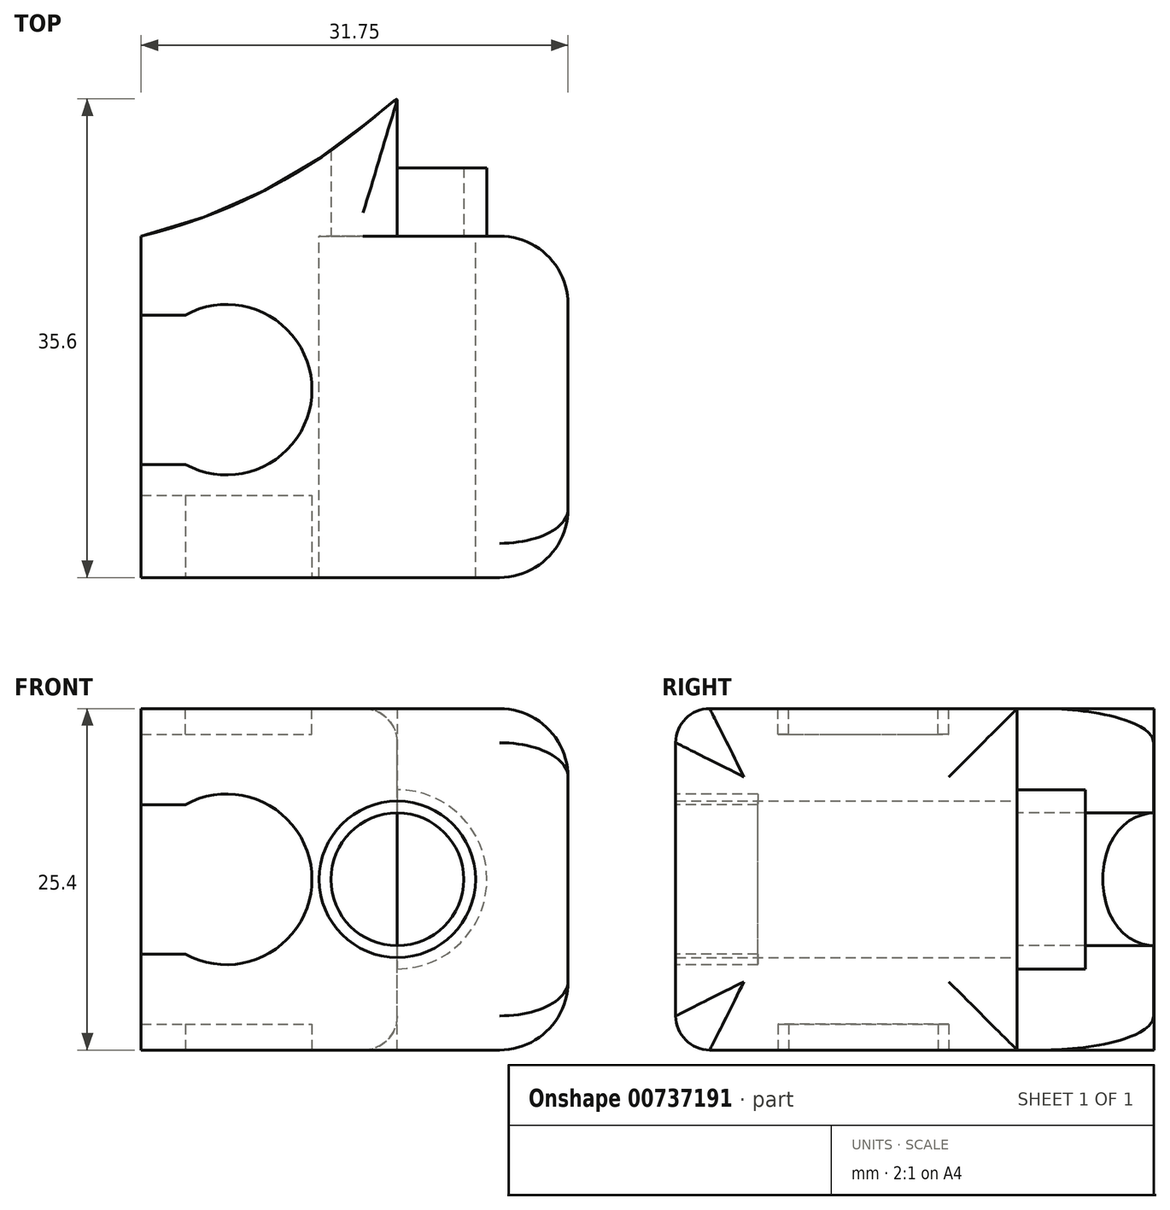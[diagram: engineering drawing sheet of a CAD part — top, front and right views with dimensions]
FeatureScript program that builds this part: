
annotation { "Feature Type Name" : "Feature", "Feature Type Description" : "" }
export const myFeature = defineFeature(function(context is Context, id is Id, definition is map)
    precondition{}
    {
        {
            var Q0;
            Q0=qCreatedBy(makeId("Front.planeOp"),FACE);
            var sketch = newSketch(context, id + "F0", { "sketchPlane" : qUnion([Q0])});
            skCircle(sketch, "E0", {"center": v(0, 0) * mm, "radius": 5.82 * mm});
            skLineSegment(sketch, "E1.bottom", {"start": v(12.7, -12.7) * mm, "end": v(-19.05, -12.7) * mm});
            skLineSegment(sketch, "E1.top", {"start": v(12.7, 12.7) * mm, "end": v(-19.05, 12.7) * mm});
            skLineSegment(sketch, "E1.left", {"start": v(12.7, -12.7) * mm, "end": v(12.7, 12.7) * mm});
            skLineSegment(sketch, "E1.right", {"start": v(-19.05, -12.7) * mm, "end": v(-19.05, 12.7) * mm});
            skPoint(sketch, "E1.middle", {"position": v(-3.17, 0) * mm});
            skSolve(sketch);
        }
        {
            var Q0;
            Q0 = qSketchRegion(id + "F0", true);
            extrude(context, id + "F1", {"entities" : qUnion([Q0]), "depth" : 25.4 * mm, "offsetDistance" : 25.4 * mm});
        }
        {
            var Q0;
            Q0=makeQuery(id+"F1.opExtrude","SWEPT_FACE",FACE,{"disambiguationData":[OSD([sQuery(id+"F0.wireOp",EDGE,"E1.top")])]});
            var sketch = newSketch(context, id + "F2", { "sketchPlane" : qUnion([Q0])});
            skFitSpline(sketch, "E2", {"points": [v(-19.05, 0) * mm, v(-4.14, 6.93) * mm, v(0, 10.16) * mm], "startDerivative": vector(25.72, 5.8) * mm, "endDerivative": vector(-0.78, -2.59) * mm});
            skLineSegment(sketch, "E3", {"start": v(0, 10.16) * mm, "end": v(0, 0) * mm});
            skLineSegment(sketch, "E4", {"start": v(0, 0) * mm, "end": v(-19.05, 0) * mm});
            skSolve(sketch);
        }
        {
            var Q0;
            Q0 = qSketchRegion(id + "F2", true);
            extrude(context, id + "F3", {"entities" : qUnion([Q0]), "operationType" : NewBodyOperationType.ADD, "oppositeDirection" : true, "depth" : 25.4 * mm, "offsetDistance" : 25.4 * mm});
        }
        {
            var Q0;
            Q0=makeQuery(id+"F1.opExtrude","CAP_FACE",FACE,{"disambiguationData":[OSD([sQuery(id+"F0.wireOp",EDGE,"E0"),sQuery(id+"F0.wireOp",EDGE,"E1.bottom"),sQuery(id+"F0.wireOp",EDGE,"E1.top"),sQuery(id+"F0.wireOp",EDGE,"E1.left"),sQuery(id+"F0.wireOp",EDGE,"E1.right")])],"isStart":true});
            var sketch = newSketch(context, id + "F4", { "sketchPlane" : qUnion([Q0])});
            skCircle(sketch, "E5", {"center": v(0, 0) * mm, "radius": 4.94 * mm});
            skCircle(sketch, "E6", {"center": v(0, 0) * mm, "radius": 6.67 * mm});
            skSolve(sketch);
        }
        {
            var Q0;
            Q0 = qSketchRegion(id + "F4", true);
            extrude(context, id + "F5", {"entities" : qUnion([Q0]), "operationType" : NewBodyOperationType.ADD, "depth" : 5.08 * mm, "offsetDistance" : 25.4 * mm});
        }
        {
            var Q0;
            Q0=makeQuery(id+"F5.opExtrude","CAP_FACE",FACE,{"disambiguationData":[OSD([sQuery(id+"F4.wireOp",EDGE,"E5"),sQuery(id+"F4.wireOp",EDGE,"E6")])],"isStart":false});
            var sketch = newSketch(context, id + "F6", { "sketchPlane" : qUnion([Q0])});
            skCircle(sketch, "E7", {"center": v(0, 0) * mm, "radius": 4.94 * mm});
            skSolve(sketch);
        }
        {
            var Q0;
            Q0 = qSketchRegion(id + "F6", true);
            extrude(context, id + "F7", {"entities" : qUnion([Q0]), "operationType" : NewBodyOperationType.REMOVE, "endBound" : BoundingType.SYMMETRIC, "oppositeDirection" : true, "depth" : 50.8 * mm, "offsetDistance" : 25.4 * mm});
        }
        {
            var Q0;
            Q0=makeQuery(id+"F1.opExtrude","CAP_EDGE",EDGE,{"disambiguationData":[OSD([sQuery(id+"F0.wireOp",EDGE,"E1.left")])],"isStart":true});
            var Q1;
            Q1=makeQuery(id+"F1.opExtrude","SWEPT_EDGE",EDGE,{"disambiguationData":[OSD([sQuery(id+"F0.wireOp",EDGE,"E1.top"),sQuery(id+"F0.wireOp",EDGE,"E1.left")])]});
            var Q2;
            Q2=makeQuery(id+"F1.opExtrude","SWEPT_EDGE",EDGE,{"disambiguationData":[OSD([sQuery(id+"F0.wireOp",EDGE,"E1.bottom"),sQuery(id+"F0.wireOp",EDGE,"E1.left")])]});
            var Q3;
            Q3=makeQuery(id+"F1.opExtrude","CAP_EDGE",EDGE,{"disambiguationData":[OSD([sQuery(id+"F0.wireOp",EDGE,"E1.left")])],"isStart":false});
            fillet(context, id + "F8", {"entities" : qUnion([Q0, Q1, Q2, Q3]), "radius" : 5.08 * mm, "tangentPropagation" : true, "allowEdgeOverflow" : false});
        }
        {
            var Q0;
            Q0=makeQuery(id+"F3.opExtrude","CAP_EDGE",EDGE,{"disambiguationData":[OSD([sQuery(id+"F2.wireOp",EDGE,"E3")])],"isStart":true});
            var Q1;
            Q1=makeQuery(id+"F3.opExtrude","CAP_EDGE",EDGE,{"disambiguationData":[OSD([sQuery(id+"F2.wireOp",EDGE,"E3")])],"isStart":false});
            var Q2;
            Q2=makeQuery(id+"F1.opExtrude","CAP_EDGE",EDGE,{"disambiguationData":[OSD([sQuery(id+"F0.wireOp",EDGE,"E1.top")])],"isStart":false});
            var Q3;
            Q3=makeQuery(id+"F1.opExtrude","CAP_EDGE",EDGE,{"disambiguationData":[OSD([sQuery(id+"F0.wireOp",EDGE,"E1.bottom")])],"isStart":false});
            fillet(context, id + "F9", {"entities" : qUnion([Q0, Q1, Q2, Q3]), "radius" : 2.54 * mm, "tangentPropagation" : true, "allowEdgeOverflow" : false});
        }
        {
            var Q0;
            Q0=makeQuery(id+"F1.opExtrude","CAP_FACE",FACE,{"disambiguationData":[OSD([sQuery(id+"F0.wireOp",EDGE,"E0"),sQuery(id+"F0.wireOp",EDGE,"E1.bottom"),sQuery(id+"F0.wireOp",EDGE,"E1.top"),sQuery(id+"F0.wireOp",EDGE,"E1.left"),sQuery(id+"F0.wireOp",EDGE,"E1.right")])],"isStart":false});
            var sketch = newSketch(context, id + "F10", { "sketchPlane" : qUnion([Q0])});
            skLineSegment(sketch, "E8", {"start": v(-19.05, 0) * mm, "end": v(-5.82, 0) * mm});
            skLineSegment(sketch, "E9.bottom", {"start": v(-19.05, -5.56) * mm, "end": v(-15.77, -5.56) * mm});
            skLineSegment(sketch, "E9.top", {"start": v(-19.05, 5.56) * mm, "end": v(-15.77, 5.56) * mm});
            skLineSegment(sketch, "E9.left", {"start": v(-19.05, -5.56) * mm, "end": v(-19.05, 5.56) * mm});
            skArc(sketch, "E10", {"start": v(-15.77, -5.56) * mm, "mid": v(-6.35, 0) * mm, "end": v(-15.77, 5.56) * mm});
            skSolve(sketch);
        }
        {
            var Q0;
            Q0 = qSketchRegion(id + "F10", true);
            extrude(context, id + "F11", {"entities" : qUnion([Q0]), "operationType" : NewBodyOperationType.REMOVE, "oppositeDirection" : true, "depth" : 4.3 * mm + 1.8 * mm, "offsetDistance" : 25.4 * mm});
        }
        {
            var Q0;
            Q0=makeQuery(id+"F3.boolean.opBoolean","MERGE",FACE,{"derivedFrom":[makeQuery(id+"F1.opExtrude","SWEPT_FACE",FACE,{"disambiguationData":[OSD([sQuery(id+"F0.wireOp",EDGE,"E1.top")])]}),makeQuery(id+"F3.opExtrude","CAP_FACE",FACE,{"disambiguationData":[OSD([sQuery(id+"F2.wireOp",EDGE,"E2"),sQuery(id+"F2.wireOp",EDGE,"E3"),sQuery(id+"F2.wireOp",EDGE,"E4")])],"isStart":true})]});
            var sketch = newSketch(context, id + "F12", { "sketchPlane" : qUnion([Q0])});
            skLineSegment(sketch, "E11", {"start": v(-19.05, -11.43) * mm, "end": v(7.62, -11.43) * mm});
            skLineSegment(sketch, "E12.bottom", {"start": v(-19.05, -16.99) * mm, "end": v(-15.77, -16.99) * mm});
            skLineSegment(sketch, "E12.top", {"start": v(-19.05, -5.87) * mm, "end": v(-15.77, -5.87) * mm});
            skLineSegment(sketch, "E12.left", {"start": v(-19.05, -16.99) * mm, "end": v(-19.05, -5.87) * mm});
            skArc(sketch, "E13", {"start": v(-15.77, -16.99) * mm, "mid": v(-6.35, -11.43) * mm, "end": v(-15.77, -5.87) * mm});
            skLineSegment(sketch, "E14", {"start": v(-2.54, 0) * mm, "end": v(-19.05, 0) * mm});
            skSolve(sketch);
        }
        {
            var Q0;
            Q0 = qSketchRegion(id + "F12", true);
            extrude(context, id + "F13", {"entities" : qUnion([Q0]), "operationType" : NewBodyOperationType.REMOVE, "oppositeDirection" : true, "depth" : 3 / 406.4 * mm + 0.1 * mm + 1.8 * mm, "offsetDistance" : 25.4 * mm});
        }
        {
            var Q0;
            Q0=makeQuery(id+"F1.opExtrude","SWEPT_FACE",FACE,{"disambiguationData":[OSD([sQuery(id+"F0.wireOp",EDGE,"E1.bottom")])]});
            var sketch = newSketch(context, id + "F14", { "sketchPlane" : qUnion([Q0])});
            skLineSegment(sketch, "E15", {"start": v(-19.05, 11.43) * mm, "end": v(7.62, 11.43) * mm});
            skLineSegment(sketch, "E16.bottom", {"start": v(-19.05, 5.87) * mm, "end": v(-15.77, 5.87) * mm});
            skLineSegment(sketch, "E16.top", {"start": v(-19.05, 16.99) * mm, "end": v(-15.77, 16.99) * mm});
            skLineSegment(sketch, "E16.left", {"start": v(-19.05, 5.87) * mm, "end": v(-19.05, 16.99) * mm});
            skArc(sketch, "E17", {"start": v(-15.77, 5.87) * mm, "mid": v(-6.35, 11.43) * mm, "end": v(-15.77, 16.99) * mm});
            skSolve(sketch);
        }
        {
            var Q0;
            Q0 = qSketchRegion(id + "F14", true);
            extrude(context, id + "F15", {"entities" : qUnion([Q0]), "operationType" : NewBodyOperationType.REMOVE, "oppositeDirection" : true, "depth" : 3 / 406.4 * mm + 0.1 * mm + 1.8 * mm, "offsetDistance" : 25.4 * mm});
        }
    });
